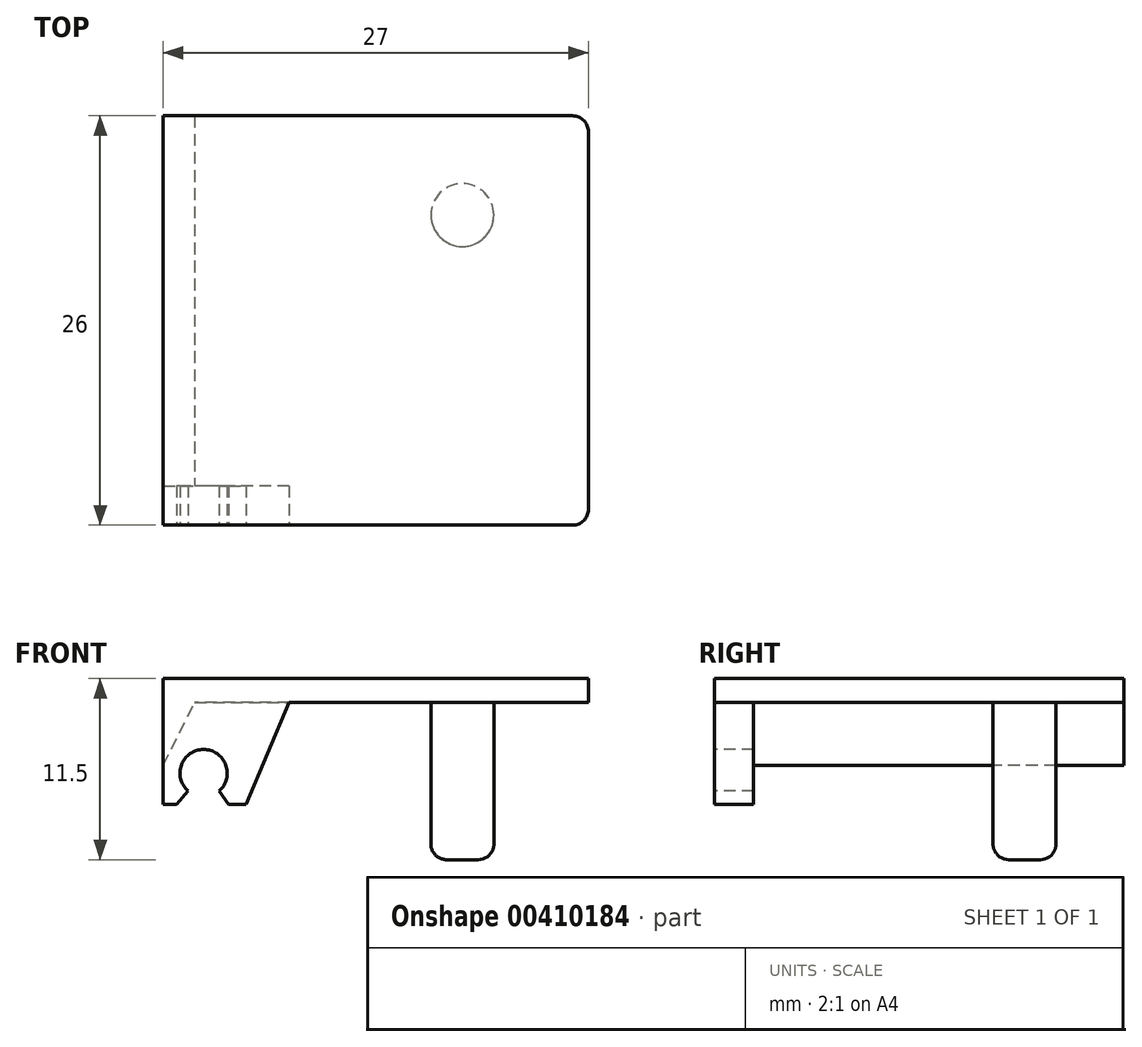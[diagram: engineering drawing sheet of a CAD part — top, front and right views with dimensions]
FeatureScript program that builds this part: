
annotation { "Feature Type Name" : "Feature", "Feature Type Description" : "" }
export const myFeature = defineFeature(function(context is Context, id is Id, definition is map)
    precondition{}
    {
        {
            var Q0;
            Q0=qCreatedBy(makeId("Top.planeOp"),FACE);
            var sketch = newSketch(context, id + "F0", { "sketchPlane" : qUnion([Q0])});
            skLineSegment(sketch, "E0.bottom", {"start": v(0, 0) * mm, "end": v(27, 0) * mm});
            skLineSegment(sketch, "E0.top", {"start": v(0, 26) * mm, "end": v(27, 26) * mm});
            skLineSegment(sketch, "E0.left", {"start": v(0, 0) * mm, "end": v(0, 26) * mm});
            skLineSegment(sketch, "E0.right", {"start": v(27, 0) * mm, "end": v(27, 26) * mm});
            skSolve(sketch);
        }
        {
            var Q0;
            Q0 = qSketchRegion(id + "F0", true);
            extrude(context, id + "F1", {"entities" : qUnion([Q0]), "depth" : 1.5 * mm});
        }
        {
            var Q0;
            Q0=qCreatedBy(makeId("Front.planeOp"),FACE);
            var sketch = newSketch(context, id + "F2", { "sketchPlane" : qUnion([Q0])});
            skLineSegment(sketch, "E1", {"start": v(0, 0) * mm, "end": v(0, -7.5) * mm});
            skLineSegment(sketch, "E2", {"start": v(8, 0) * mm, "end": v(4.84, -7.5) * mm});
            skLineSegment(sketch, "E3", {"start": v(8, 0) * mm, "end": v(0, 0) * mm});
            skLineSegment(sketch, "E4", {"start": v(2, 0) * mm, "end": v(2, -3.1) * mm});
            skLineSegment(sketch, "E5", {"start": v(3, 0) * mm, "end": v(3, -3.07) * mm});
            skCircle(sketch, "E6", {"center": v(2.56, -4.5) * mm, "radius": 1.5 * mm});
            skLineSegment(sketch, "E7", {"start": v(3.56, -5.62) * mm, "end": v(4.84, -7.5) * mm});
            skLineSegment(sketch, "E8", {"start": v(1.57, -5.62) * mm, "end": v(0, -7.5) * mm});
            skLineSegment(sketch, "E9", {"start": v(0, -6.5) * mm, "end": v(0.84, -6.5) * mm});
            skLineSegment(sketch, "E10", {"start": v(4.15, -6.5) * mm, "end": v(5.26, -6.5) * mm});
            skSolve(sketch);
        }
        {
            var Q0;
            {var subQ0=sQuery(id+"F2.wireOp",EDGE,"E4");Q0=makeQuery(id+"F2.imprint","IMPRINT",FACE,{"disambiguationData":[TD([[makeQuery(id+"F2.imprint","IMPRINT",EDGE,{"derivedFrom":subQ0}),-1.0]])]});}
            var Q1;
            {var subQ0=sQuery(id+"F2.wireOp",EDGE,"E5");Q1=makeQuery(id+"F2.imprint","IMPRINT",FACE,{"disambiguationData":[TD([[makeQuery(id+"F2.imprint","IMPRINT",EDGE,{"derivedFrom":subQ0}),1.0]])]});}
            var Q2;
            {var subQ0=sQuery(id+"F2.wireOp",EDGE,"E4");Q2=makeQuery(id+"F2.imprint","IMPRINT",FACE,{"disambiguationData":[TD([[makeQuery(id+"F2.imprint","IMPRINT",EDGE,{"derivedFrom":subQ0}),1.0]])]});}
            extrude(context, id + "F3", {"entities" : qUnion([Q0, Q1, Q2]), "operationType" : NewBodyOperationType.ADD, "oppositeDirection" : true, "depth" : 2.5 * mm});
        }
        {
            var Q0;
            Q0=qCreatedBy(makeId("Front.planeOp"),FACE);
            var sketch = newSketch(context, id + "F4", { "sketchPlane" : qUnion([Q0])});
            skLineSegment(sketch, "E11", {"start": v(0, 0) * mm, "end": v(0, -4) * mm});
            skLineSegment(sketch, "E12", {"start": v(0, -4) * mm, "end": v(2, 0) * mm});
            skLineSegment(sketch, "E13", {"start": v(2, 0) * mm, "end": v(0, 0) * mm});
            skSolve(sketch);
        }
        {
            var Q0;
            Q0 = qSketchRegion(id + "F4", true);
            var Q1;
            Q1=makeQuery(id+"F1.opExtrude","SWEPT_FACE",FACE,{"disambiguationData":[OSD([sQuery(id+"F0.wireOp",EDGE,"E0.top")])]});
            extrude(context, id + "F5", {"entities" : qUnion([Q0]), "operationType" : NewBodyOperationType.ADD, "endBound" : BoundingType.UP_TO_SURFACE, "oppositeDirection" : true, "endBoundEntityFace" : qUnion([Q1]), "depth" : 25 * mm});
        }
        {
            var Q0;
            {var subQ0=sQuery(id+"F0.wireOp",EDGE,"E0.top");Q0=makeQuery(id+"F5.boolean.opBoolean","MERGE",FACE,{"derivedFrom":[makeQuery(id+"F1.opExtrude","SWEPT_FACE",FACE,{"disambiguationData":[OSD([subQ0])]}),makeQuery(id+"F5.opExtrude","CAP_FACE",FACE,{"disambiguationData":[OSD([subQ0])],"isStart":false})]});}
            var Q1;
            {var subQ0=sQuery(id+"F2.wireOp",EDGE,"E6");var subQ1=sQuery(id+"F2.wireOp",EDGE,"E3");Q1=makeQuery(id+"F3.boolean.opBoolean","MERGE",FACE,{"derivedFrom":[makeQuery(id+"F1.opExtrude","SWEPT_FACE",FACE,{"disambiguationData":[OSD([sQuery(id+"F0.wireOp",EDGE,"E0.bottom")])]}),makeQuery(id+"F3.opExtrude","CAP_FACE",FACE,{"disambiguationData":[OSD([sQuery(id+"F2.wireOp",EDGE,"E1"),subQ1,sQuery(id+"F2.wireOp",EDGE,"E4"),subQ0,sQuery(id+"F2.wireOp",EDGE,"E8")])],"isStart":true}),makeQuery(id+"F3.opExtrude","CAP_FACE",FACE,{"disambiguationData":[OSD([sQuery(id+"F2.wireOp",EDGE,"E2"),subQ1,sQuery(id+"F2.wireOp",EDGE,"E5"),subQ0,sQuery(id+"F2.wireOp",EDGE,"E7")])],"isStart":true})]});}
            cPlane(context, id + "F6", {"entities" : qUnion([Q0, Q1]), "cplaneType" : CPlaneType.MID_PLANE, "offset" : 25 * mm, "width" : 150 * mm, "height" : 150 * mm});
        }
        {
            var Q0;
            Q0=makeQuery(id+"F1.opExtrude","CAP_FACE",FACE,{"disambiguationData":[OSD([sQuery(id+"F0.wireOp",EDGE,"E0.bottom"),sQuery(id+"F0.wireOp",EDGE,"E0.top"),sQuery(id+"F0.wireOp",EDGE,"E0.left"),sQuery(id+"F0.wireOp",EDGE,"E0.right")])],"isStart":true});
            var sketch = newSketch(context, id + "F7", { "sketchPlane" : qUnion([Q0])});
            skCircle(sketch, "E14", {"center": v(19, -19.7) * mm, "radius": 2 * mm});
            skSolve(sketch);
        }
        {
            var Q0;
            Q0 = qSketchRegion(id + "F7", true);
            extrude(context, id + "F8", {"entities" : qUnion([Q0]), "operationType" : NewBodyOperationType.ADD, "depth" : 10 * mm});
        }
        {
            var Q0;
            Q0=makeQuery(id+"F8.opExtrude","CAP_EDGE",EDGE,{"disambiguationData":[OSD([sQuery(id+"F7.wireOp",EDGE,"E14")])],"isStart":true});
            var Q1;
            Q1=makeQuery(id+"F8.opExtrude","CAP_EDGE",EDGE,{"disambiguationData":[OSD([sQuery(id+"F7.wireOp",EDGE,"E14")])],"isStart":false});
            fillet(context, id + "F9", {"entities" : qUnion([Q0, Q1]), "radius" : 1 * mm, "allowEdgeOverflow" : false});
        }
        {
            var Q0;
            Q0=makeQuery(id+"F1.opExtrude","SWEPT_EDGE",EDGE,{"disambiguationData":[OSD([sQuery(id+"F0.wireOp",EDGE,"E0.top"),sQuery(id+"F0.wireOp",EDGE,"E0.right")])]});
            var Q1;
            Q1=makeQuery(id+"F1.opExtrude","SWEPT_EDGE",EDGE,{"disambiguationData":[OSD([sQuery(id+"F0.wireOp",EDGE,"E0.bottom"),sQuery(id+"F0.wireOp",EDGE,"E0.right")])]});
            fillet(context, id + "F10", {"entities" : qUnion([Q0, Q1]), "radius" : 1 * mm, "tangentPropagation" : true, "allowEdgeOverflow" : false});
        }
    });
